# Revit family: Gira_019000
name_source: partatom
category: Electrical Fixtures
revit_build: Autodesk Revit 2017 (Build: 20160225_1515(x64)
units: mm (PartAtom-declared; Revit-internal decimal feet)

## family parameters
Cut with Voids When Loaded = No
Host = Face
Maintain Annotation Orientation = Yes
Part Type = Normal
Room Calculation Point = No
Round Connector Dimension = Use Diameter
Shared = No

## types (1)
- Gira_019000
    Abschlusswiderstand = No
    Anschlussart = Schraube
    Aufputz = No
    Auslassrichtung = gerade
    Available = Yes
    Befestigungsart = schrauben
    Bodentank/Unterflurmontage = No
    Category = Kommunikationsanschlussdose Kupfer
    Data sheet (1) = https://katalog.gira.de
    Default Elevation = 1219 mm
    Designfähig = No
    Farbe = sonstige
    GTIN = 4010337190004
    Geeignet für Anzahl Buchsen/Kupplungen = 2
    HAN = 019000
    HeinzeBIM = https://bimportal.heinze.de
    Kanaleinbau = No
    Kategorie = 3 (*en-EN)
    Keynote = Einsatz_1fach
    Manufacturer URL = https://www.gira.de
    Mit Buchsen/Kupplungen = No
    Mit Staubschutz = No
    Mit Textfeld = No
    Name = UAE/IAE-Anschlussdose 2 x 8-p 8/8 SRK Einsatz
    Region = DE
    Schutzart (IP) = IP20
    Steckverbindertyp = sonstige
    URL = http://katalog.gira.de
    Unterputz = Yes

## geometry (parser evidence)
native form markers: Sweep x3
no freeform markers — native parametric forms only
